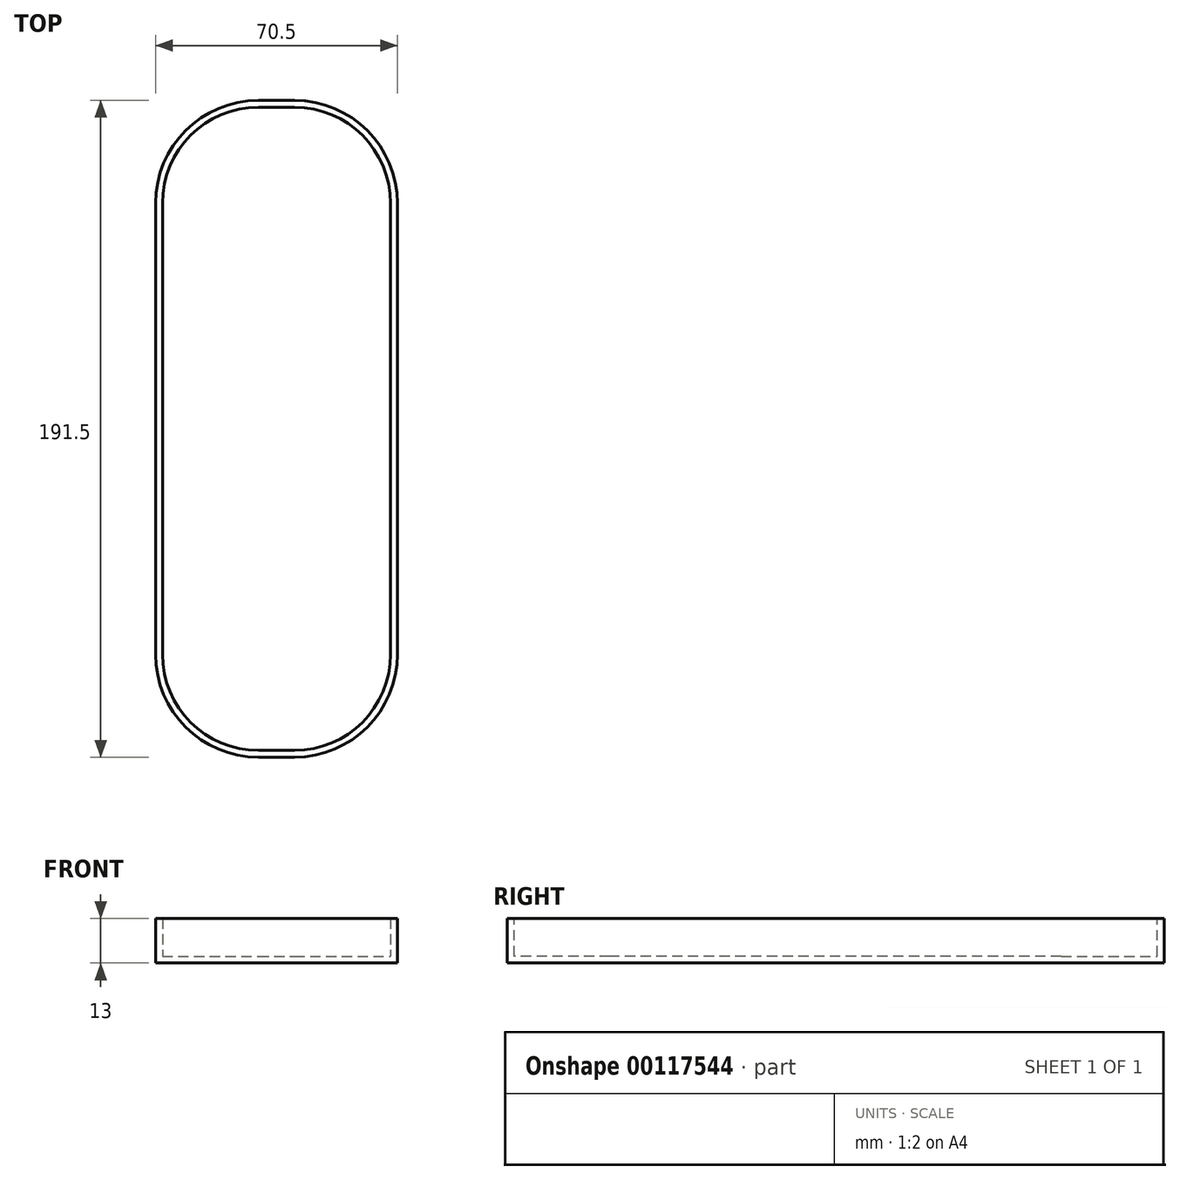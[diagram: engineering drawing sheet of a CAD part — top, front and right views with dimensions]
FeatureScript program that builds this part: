
annotation { "Feature Type Name" : "Feature", "Feature Type Description" : "" }
export const myFeature = defineFeature(function(context is Context, id is Id, definition is map)
    precondition{}
    {
        {
            var Q0;
            Q0=qCreatedBy(makeId("Top.planeOp"),FACE);
            var sketch = newSketch(context, id + "F0", { "sketchPlane" : qUnion([Q0])});
            skLineSegment(sketch, "E0.bottom", {"start": v(-5.25, 95.75) * mm, "end": v(5.25, 95.75) * mm});
            skLineSegment(sketch, "E0.top", {"start": v(-5.25, -95.75) * mm, "end": v(5.25, -95.75) * mm});
            skLineSegment(sketch, "E0.left", {"start": v(-35.25, 65.75) * mm, "end": v(-35.25, -65.75) * mm});
            skLineSegment(sketch, "E0.right", {"start": v(35.25, 65.75) * mm, "end": v(35.25, -65.75) * mm});
            skLineSegment(sketch, "E1", {"start": v(-35.25, 0) * mm, "end": v(35.25, 0) * mm, "construction": true});
            skPoint(sketch, "E2.visualSharp", {"position": v(-35.25, 95.75) * mm});
            skArc(sketch, "E2.filletArc", {"start": v(-5.25, 95.75) * mm, "mid": v(-26.46, 86.96) * mm, "end": v(-35.25, 65.75) * mm});
            skPoint(sketch, "E3.visualSharp", {"position": v(-35.25, -95.75) * mm});
            skArc(sketch, "E3.filletArc", {"start": v(-35.25, -65.75) * mm, "mid": v(-26.46, -86.96) * mm, "end": v(-5.25, -95.75) * mm});
            skPoint(sketch, "E4.visualSharp", {"position": v(35.25, -95.75) * mm});
            skArc(sketch, "E4.filletArc", {"start": v(5.25, -95.75) * mm, "mid": v(26.46, -86.96) * mm, "end": v(35.25, -65.75) * mm});
            skPoint(sketch, "E5.visualSharp", {"position": v(35.25, 95.75) * mm});
            skArc(sketch, "E5.filletArc", {"start": v(35.25, 65.75) * mm, "mid": v(26.46, 86.96) * mm, "end": v(5.25, 95.75) * mm});
            skSolve(sketch);
        }
        {
            var Q0;
            Q0=qSketchRegion(id+"F0",true);
            extrude(context, id + "F1", {"entities" : qUnion([Q0]), "depth" : 13 * mm});
        }
        {
            var Q0;
            Q0=makeQuery(id+"F1.opExtrude","CAP_FACE",FACE,{"disambiguationData":[OSD([sQuery(id+"F0.wireOp",EDGE,"E0.bottom"),sQuery(id+"F0.wireOp",EDGE,"E0.top"),sQuery(id+"F0.wireOp",EDGE,"E0.left"),sQuery(id+"F0.wireOp",EDGE,"E0.right"),sQuery(id+"F0.wireOp",EDGE,"E2.filletArc"),sQuery(id+"F0.wireOp",EDGE,"E3.filletArc"),sQuery(id+"F0.wireOp",EDGE,"E4.filletArc"),sQuery(id+"F0.wireOp",EDGE,"E5.filletArc")])],"isStart":false});
            shell(context, id + "F2", {"entities" : qUnion([Q0]), "thickness" : 2 * mm});
        }
    });
